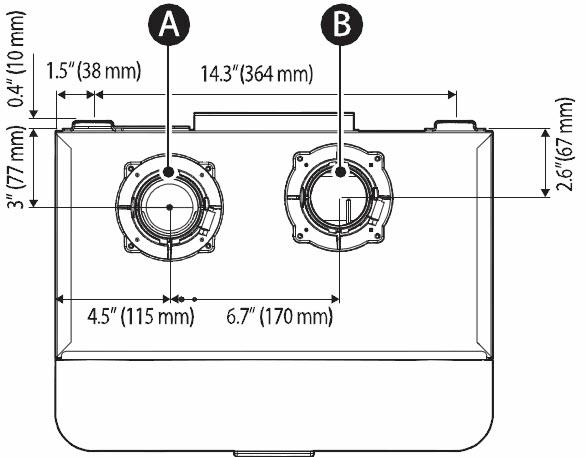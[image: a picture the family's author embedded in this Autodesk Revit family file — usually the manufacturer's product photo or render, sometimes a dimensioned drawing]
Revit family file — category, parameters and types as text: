
# Revit family: Water_Heater-Racks-Navien-NPE-3_Unit_Front-Wall-02
name_source: partatom
category: Mechanical Equipment
revit_build: Autodesk Revit 2016 (Build: 20150220_1215(x64)
units: mm (PartAtom-declared; Revit-internal decimal feet)

## family parameters
Cut with Voids When Loaded = No
Host = Face
OmniClass Number = 23.65.35.11
OmniClass Title = Supply Water Heaters
Part Type = Normal
Room Calculation Point = No
Round Connector Dimension = Use Diameter
Shared = No

## types (4) — shared parameters
2" Exhaust/Intake = Yes
3" Exhaust/Intake = No
Apparent Load = 0 VA
Assembly Code = D3010500
Certifications = Energy Star | AHRI | CSA | CSA | NFS
Cold Water Inlet = 1"
Configuration = NPE_F3_3F
Default Elevation = 48 "
Depth = 23.8 "
Description = 3 Unit Front
Exhaust = 2"
Finish = Metal - Navien - White
Flow Rate = 1 GPM
Flow Rate Note = 35°F (19°C) temp rise: 11.2 GPM (42 L/m) | 45°F (25°C) temp rise: 8.7 GPM (33 L/m) | 67°F (36°C) temp rise: NPE-240A: 5.6 GPM(21 L/m), NPE-240S: 5.7 GPM(22 L/m)
Frequency = 60 Hz
Gas Inlet = 1"
Heating Capacity = 120000.0 Btu/h
Heating Capacity Note = 19,900–199,900 (BTU/H)
Height = 65.5 "
Hot Water Outlet = 1"
Ignition = Electronic ignition
Installation Type = Indoor
Intake = 2"
Keynote = 22 33 00.A1
Manifold(s) = (1) 30019041A
Manufacturer = Navien, Inc.
Manufacturer Fax Number = (949) 420-0430
Natural Gas Manifold Pressure = -0.05" WC to -0.58" WC
Natural Gas Supply Pressure = 3.5"–10.5" WC
Number of Poles = 1
Phase = 1
Power Factor = 1
Product Documentation Link = https://www.navieninc.com
Product Name = NPE Series Tankless Water Heaters w/ Racks
Product Page URL = https://www.navieninc.com
Propane Gas Manifold Pressure = -0.10" WC to -0.78" WC
Propane Gas Supply Pressure = 8"–13" WC
Required Cascade Operation Accessory = (3) 30014367A (Common Vent Damper & Cascade Communication Cable) or (2) GXXX000546 (Individual Vent Cascade Communication Cable)
Type Comments = For Wall Mount RL Manifold systems- Exclude Base & Add-on Racks
URL = https://www.navieninc.com
Venting = Exhaust: 2" PVC, CPVC, PP, SS / 2" special gas vent type BH (Class II, A/B/C) | Intake: 2" PVC, CPVC, PP, SS / 2" special gas vent type BH (Class II, A/B/C) | Vent clearances: 0" to combustibles
Venting Type = Forced draft direct vent
Version = 2016 - v1.0.a
Voltage = 120 V
Water Pressure = 15–150 PSI
Wi-Fi Ready = NaviLink Wi-Fi Control: PBCM-AS-001
Width = 62.3 "

## per-type parameters (varying)
| type | Constraints | Model | Natural Gas | Propane Gas | Recirculation Inlet | Recirculation Inlet Visibility | Tankless Water Heaters | Weight |
| Natural Gas - Recirculating System - NPE-240A(Advanced)-NG | 6 | (3) NPE-240A-NG | Yes | No | 0" | Yes | (3) NPE-240A-NG | 82.00 lbf |
| Natural Gas - NPE-240S(Standard)-NG | 7 | (3) NPE-240S-NG | Yes | No | 1" | No | (3) NPE-240S-NG | 75.00 lbf |
| Propane Gas - Recirculating System - NPE-240A(Advanced)-LPG | 6 | (3) NPE-240A-LPG | No | Yes | 0" | Yes | (3) NPE-240A-LPG | 82.00 lbf |
| Propane Gas - NPE-240S(Standard)-LPG | 7 | (3) NPE-240S-LPG | No | Yes | 1" | No | (3) NPE-240S-LPG | 75.00 lbf |

## geometry (parser evidence)
native form markers: Sweep x12
no freeform markers — native parametric forms only
